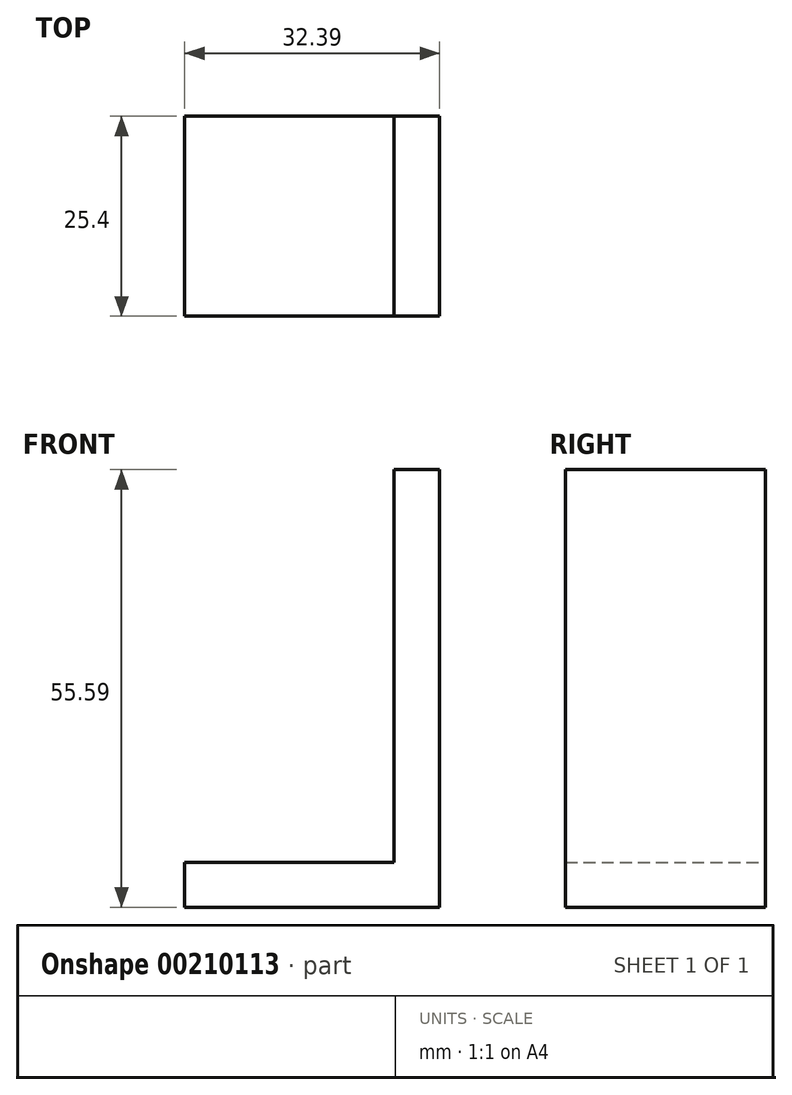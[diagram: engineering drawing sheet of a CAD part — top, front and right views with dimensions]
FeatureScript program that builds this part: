
annotation { "Feature Type Name" : "Feature", "Feature Type Description" : "" }
export const myFeature = defineFeature(function(context is Context, id is Id, definition is map)
    precondition{}
    {
        {
            var Q0;
            Q0=qCreatedBy(makeId("Front.planeOp"),FACE);
            var sketch = newSketch(context, id + "F0", { "sketchPlane" : qUnion([Q0])});
            skLineSegment(sketch, "E0", {"start": v(-5.82, 0) * mm, "end": v(-5.82, -49.89) * mm});
            skLineSegment(sketch, "E1", {"start": v(-5.82, -49.89) * mm, "end": v(-32.4, -49.89) * mm});
            skLineSegment(sketch, "E2", {"start": v(-32.4, -49.89) * mm, "end": v(-32.4, -55.6) * mm});
            skLineSegment(sketch, "E3", {"start": v(-32.4, -55.6) * mm, "end": v(0, -55.6) * mm});
            skLineSegment(sketch, "E4", {"start": v(0, -55.6) * mm, "end": v(0, 0) * mm});
            skLineSegment(sketch, "E5", {"start": v(0, 0) * mm, "end": v(-5.82, 0) * mm});
            skSolve(sketch);
        }
        {
            var Q0;
            Q0=makeQuery(id+"F0.imprint","IMPRINT",FACE,{"disambiguationData":[TD([[makeQuery(id+"F0.imprint","IMPRINT",EDGE,{"derivedFrom":sQuery(id+"F0.wireOp",EDGE,"E0")}),1.0]])]});
            extrude(context, id + "F1", {"entities" : qUnion([Q0]), "depth" : 25.4 * mm});
        }
    });
